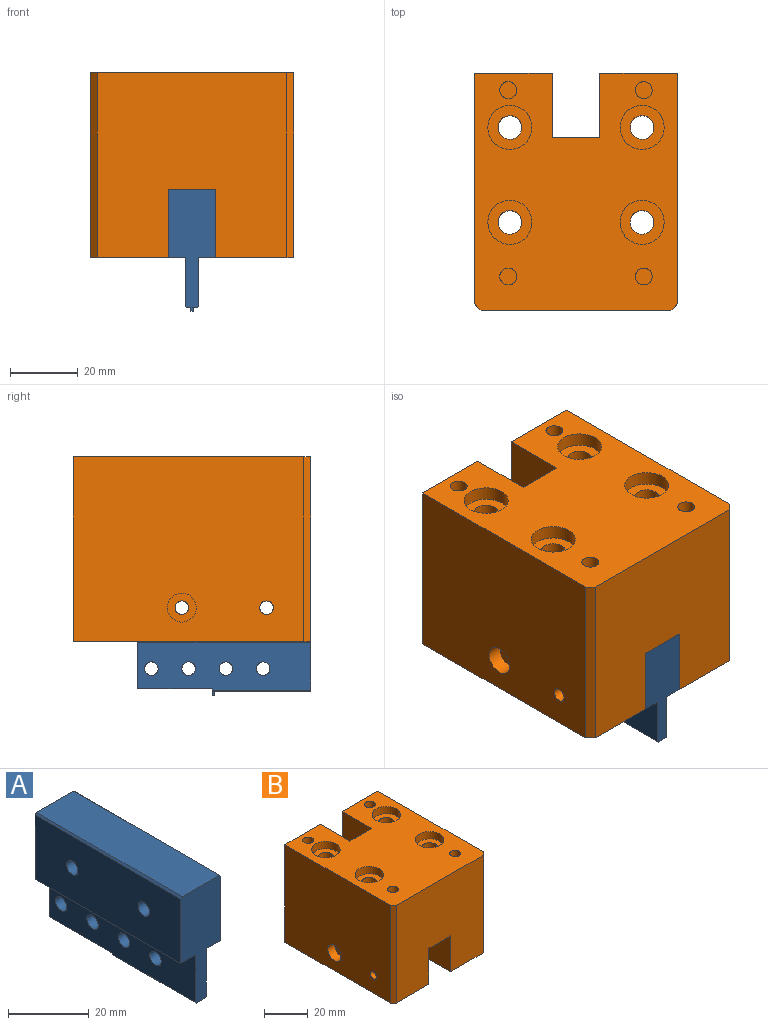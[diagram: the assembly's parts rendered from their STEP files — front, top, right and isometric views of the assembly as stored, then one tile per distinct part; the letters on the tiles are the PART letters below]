
ASSEMBLY  parts=2 mates=1
PART A: 32 faces, bbox 14x51x35.9 mm
  f0: plane 33.9x14mm, normal (0,1,0), area 307.5mm2, adj f4,f5,f7,f8,f10,f17,f18,f21
  f1: plane 0.7x0.6mm, normal (0,0,-1), area 0.4mm2, adj f2,f3,f11,f12
  f2: plane 1.2x0.7mm, normal (0,-1,0), area 0.8mm2, adj f1,f9,f11,f12
  f3: plane 3.8x1.95mm, normal (0,1,0), area 3.6mm2, adj f1,f4,f5,f9,f10,f11,f12,f19
  f4: plane 51.03x14.15mm, normal (1,0,0), area 661.8mm2, adj f0,f3,f6,f10,f13,f14,f15,f16
  f5: plane 51.03x14.15mm, normal (-1,0,0), area 661.8mm2, adj f0,f3,f6,f10,f13,f14,f15,f16
  f6: plane 34.65x14mm, normal (0,-1,0), area 335.3mm2, adj f4,f5,f7,f8,f9,f17,f18,f19
  f7: plane 51.03x4.9mm, normal (0,0,-1), area 250mm2, adj f0,f6,f17,f26
  f8: plane 51.03x4.9mm, normal (0,0,-1), area 250mm2, adj f0,f6,f18,f25
  f9: plane 28.98x3.2mm, normal (0,0,-1), area 92.3mm2, adj f2,f3,f6,f11,f12,f19,f20
  f10: plane 22.05x3.8mm, normal (0,0,-1), area 83.8mm2, adj f0,f3,f4,f5
  f11: plane 1.2x0.6mm, normal (1,0,0), area 0.7mm2, adj f1,f2,f3,f9
  f12: plane 1.2x0.6mm, normal (-1,0,0), area 0.7mm2, adj f1,f2,f3,f9
  f13: cylinder r=2mm len=4mm, axis (-1,0,0), area 47.8mm2, adj f4,f5
  f14: cylinder r=2mm len=4mm, axis (-1,0,0), area 47.8mm2, adj f4,f5
  f15: cylinder r=2mm len=4mm, axis (-1,0,0), area 47.8mm2, adj f4,f5
  f16: cylinder r=2mm len=4mm, axis (-1,0,0), area 47.8mm2, adj f4,f5
  f17: cylinder r=0.2mm len=51.03mm, axis (0,-1,0), area 16mm2, adj f0,f4,f6,f7
  f18: cylinder r=0.2mm len=51.03mm, axis (0,-1,0), area 16mm2, adj f0,f5,f6,f8
  f19: plane 28.98x0.3mm, normal (0.71,0,-0.71), area 12.3mm2, adj f3,f4,f6,f9
  f20: plane 28.98x0.3mm, normal (-0.71,0,-0.71), area 12.3mm2, adj f3,f5,f6,f9
  f21: cylinder r=2mm len=10mm, axis (0,1,0), area 125.7mm2, adj f0,f22
  f22: plane 4x4mm, normal (0,1,0), area 12.6mm2, adj f21
  f23: cylinder r=2mm len=10mm, axis (0,1,0), area 125.7mm2, adj f0,f24
  f24: plane 4x4mm, normal (0,1,0), area 12.6mm2, adj f23
  f25: plane 51.03x19.5mm, normal (-1,0,0), area 969.9mm2, adj f0,f6,f8,f28,f29,f31
  f26: plane 51.03x19.5mm, normal (1,0,0), area 969.9mm2, adj f0,f6,f7,f28,f29,f30
  f27: plane 51.03x13mm, normal (0,0,1), area 663.3mm2, adj f0,f6,f30,f31
  f28: cylinder r=2mm len=14mm, axis (1,0,0), area 175.9mm2, adj f25,f26
  f29: cylinder r=2mm len=14mm, axis (1,0,0), area 175.9mm2, adj f25,f26
  f30: plane 51.03x0.5mm, normal (0.71,0,0.71), area 36.1mm2, adj f0,f6,f26,f27
  f31: plane 51.03x0.5mm, normal (-0.71,0,0.71), area 36.1mm2, adj f0,f6,f25,f27
PART B: 48 faces, bbox 60x70x54.6 mm
  f0: cylinder r=2mm len=18.5mm, axis (1,0,0), area 232.5mm2, adj f16,f40
  f1: cylinder r=2mm len=18.5mm, axis (1,0,0), area 232.5mm2, adj f15,f38
  f2: plane 70x23mm, normal (0,0,-1), area 1531mm2, adj f4,f5,f9,f12,f13,f16,f34
  f3: plane 34.55x14mm, normal (0,1,0), area 446mm2, adj f11,f15,f16,f35,f42,f44,f46
  f4: cylinder r=3.5mm len=50.45mm, axis (0,0,1), area 1109.5mm2, adj f2,f23
  f5: cylinder r=3.5mm len=50.45mm, axis (0,0,1), area 1109.5mm2, adj f2,f21
  f6: cylinder r=3.5mm len=50.45mm, axis (0,0,1), area 1109.5mm2, adj f14,f19
  f7: cylinder r=3.5mm len=50.45mm, axis (0,0,1), area 1109.5mm2, adj f14,f17
  f8: plane 54.55x23mm, normal (0,1,0), area 1254.6mm2, adj f10,f11,f14,f15
  f9: plane 56x54.55mm, normal (0,-1,0), area 2774.8mm2, adj f2,f11,f14,f15,f16,f33,f34,f35
  f10: plane 68x54.55mm, normal (1,0,0), area 3640.1mm2, adj f8,f11,f14,f33,f37,f39
  f11: plane 70x60mm, normal (0,0,1), area 3320.9mm2, adj f3,f8,f9,f10,f12,f13,f15,f16
  f12: plane 68x54.55mm, normal (-1,0,0), area 3640.1mm2, adj f2,f11,f13,f34,f36,f41
  f13: plane 54.55x23mm, normal (0,1,0), area 1254.6mm2, adj f2,f11,f12,f16
  f14: plane 70x23mm, normal (0,0,-1), area 1531mm2, adj f6,f7,f8,f9,f10,f15,f33
  f15: plane 70x54.55mm, normal (-1,0,0), area 2030.5mm2, adj f1,f3,f8,f9,f11,f14,f35,f37
  f16: plane 70x54.55mm, normal (1,0,0), area 2030.5mm2, adj f0,f2,f3,f9,f11,f13,f35,f36
  f17: plane 13x13mm, normal (0,0,1), area 94.2mm2, adj f7,f18
  f18: cylinder r=6.5mm len=13mm, axis (0,0,1), area 167.4mm2, adj f11,f17
  f19: plane 13x13mm, normal (0,0,1), area 94.2mm2, adj f6,f20
  f20: cylinder r=6.5mm len=13mm, axis (0,0,1), area 167.4mm2, adj f11,f19
  f21: plane 13x13mm, normal (0,0,1), area 94.2mm2, adj f5,f22
  f22: cylinder r=6.5mm len=13mm, axis (0,0,1), area 167.4mm2, adj f11,f21
  f23: plane 13x13mm, normal (0,0,1), area 94.2mm2, adj f4,f24
  f24: cylinder r=6.5mm len=13mm, axis (0,0,1), area 167.4mm2, adj f11,f23
  f25: cylinder r=2.5mm len=15mm, axis (0,0,1), area 235.6mm2, adj f11,f26
  f26: plane 5x5mm, normal (0,0,1), area 19.6mm2, adj f25
  f27: cylinder r=2.5mm len=15mm, axis (0,0,1), area 235.6mm2, adj f11,f28
  f28: plane 5x5mm, normal (0,0,1), area 19.6mm2, adj f27
  f29: cylinder r=2.5mm len=15mm, axis (0,0,1), area 235.6mm2, adj f11,f30
  f30: plane 5x5mm, normal (0,0,1), area 19.6mm2, adj f29
  f31: cylinder r=2.5mm len=15mm, axis (0,0,1), area 235.6mm2, adj f11,f32
  f32: plane 5x5mm, normal (0,0,1), area 19.6mm2, adj f31
  f33: plane 54.55x2mm, normal (0.71,-0.71,0), area 154.3mm2, adj f9,f10,f11,f14
  f34: plane 54.55x2mm, normal (-0.71,-0.71,0), area 154.3mm2, adj f2,f9,f11,f12
  f35: plane 51.03x14mm, normal (0,0,-1), area 714.4mm2, adj f3,f9,f15,f16
  f36: cylinder r=2mm len=23mm, axis (1,0,0), area 289mm2, adj f12,f16
  f37: cylinder r=2mm len=23mm, axis (1,0,0), area 289mm2, adj f10,f15
  f38: plane 8.5x8.5mm, normal (1,0,0), area 44.2mm2, adj f1,f39
  f39: cylinder r=4.25mm len=8.5mm, axis (1,0,0), area 120.2mm2, adj f10,f38
  f40: plane 8.5x8.5mm, normal (-1,0,0), area 44.2mm2, adj f0,f41
  f41: cylinder r=4.25mm len=8.5mm, axis (-1,0,0), area 120.2mm2, adj f12,f40
  f42: cylinder r=2mm len=10mm, axis (0,1,0), area 125.7mm2, adj f3,f43
  f43: plane 4x4mm, normal (0,1,0), area 12.6mm2, adj f42
  f44: cylinder r=2mm len=10mm, axis (0,1,0), area 125.7mm2, adj f3,f45
  f45: plane 4x4mm, normal (0,1,0), area 12.6mm2, adj f44
  f46: cylinder r=2mm len=10mm, axis (0,1,0), area 125.7mm2, adj f3,f47
  f47: plane 4x4mm, normal (0,1,0), area 12.6mm2, adj f46
PLACE A t=(-68.54,-72.65,-5.05)mm
PLACE B t=(-68.54,-72.65,-5.05)mm
MATE fastened A.f29 <-> B.f41  axis (1,0,0) through (-61.54,-34.65,-14.4)mm
